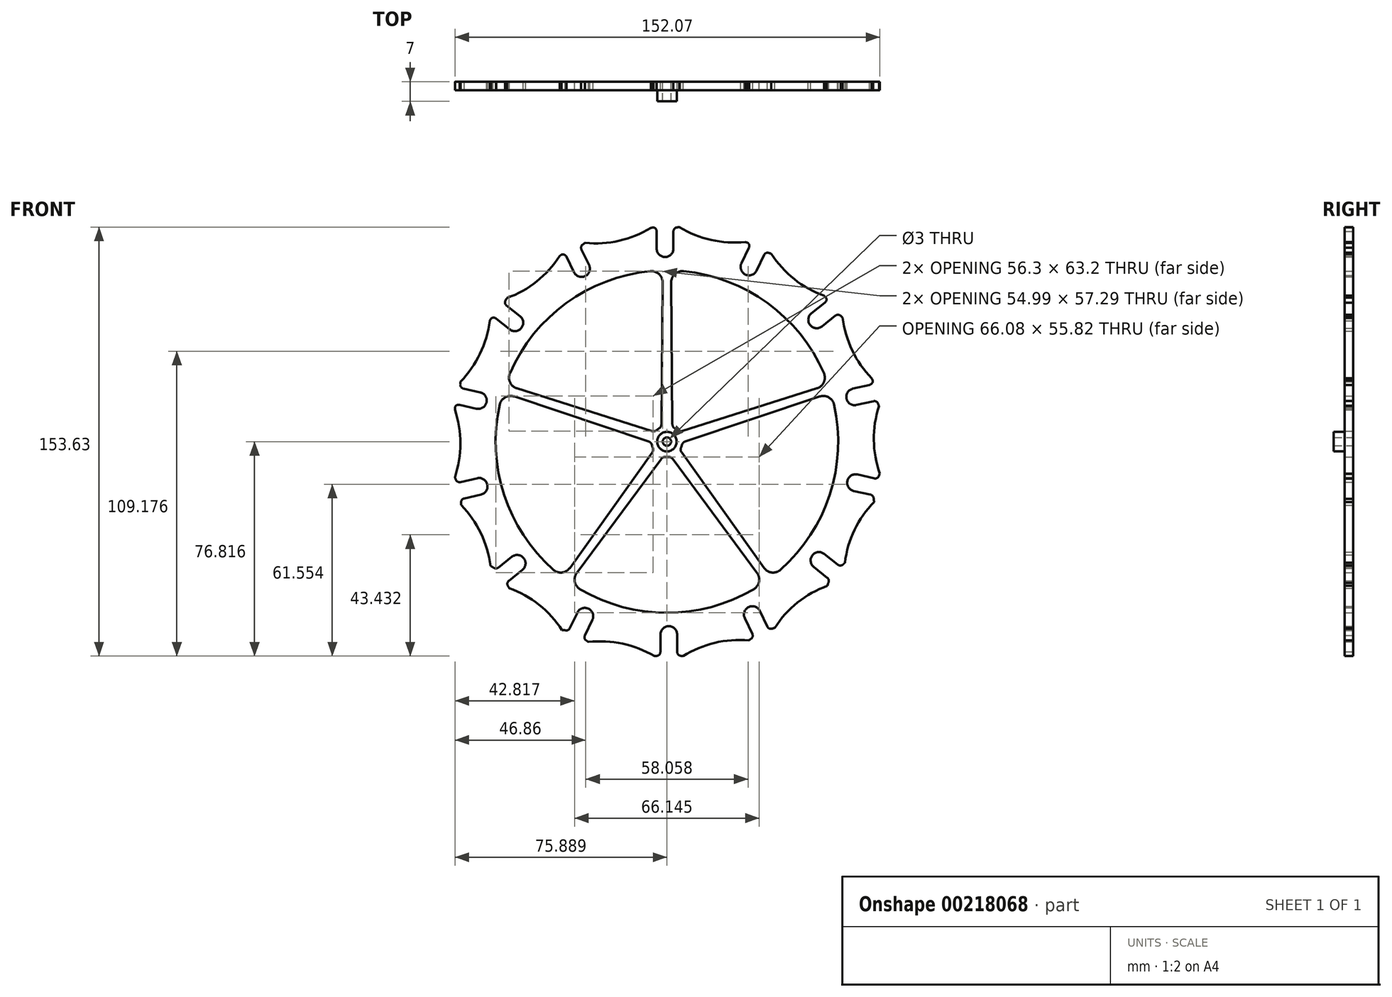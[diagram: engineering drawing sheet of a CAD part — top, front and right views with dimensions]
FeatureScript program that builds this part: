
annotation { "Feature Type Name" : "Feature", "Feature Type Description" : "" }
export const myFeature = defineFeature(function(context is Context, id is Id, definition is map)
    precondition{}
    {
        {
            var Q0;
            Q0=qCreatedBy(makeId("Front.planeOp"),FACE);
            var sketch = newSketch(context, id + "F0", { "sketchPlane" : qUnion([Q0])});
            skCircle(sketch, "E0", {"center": v(-22.2, -31.98) * mm, "radius": 2 * mm});
            skCircle(sketch, "E1", {"center": v(-22.2, -71.34) * mm, "radius": 1.5 * mm});
            skPoint(sketch, "E2.startSnap0", {"position": v(-22.24, -28.34) * mm});
            skPoint(sketch, "E3.orphan", {"position": v(-21.48, -28.34) * mm});
            skCircle(sketch, "E4", {"center": v(-22.2, -71.34) * mm, "radius": 7.5 * mm});
            skCircle(sketch, "E5", {"center": v(-22.2, -71.34) * mm, "radius": 2.5 * mm});
            skArc(sketch, "E6", {"start": v(-26.44, -36.03) * mm, "mid": v(-26.89, -36.09) * mm, "end": v(-27.34, -36.15) * mm});
            skArc(sketch, "E7.1.1", {"start": v(7.2, -29.99) * mm, "mid": v(6.81, -30.23) * mm, "end": v(6.43, -30.49) * mm});
            skArc(sketch, "E7.2.1", {"start": v(34.87, -9.95) * mm, "mid": v(34.73, -10.46) * mm, "end": v(34.6, -10.96) * mm});
            skArc(sketch, "E7.4.1", {"start": v(52.7, 54.24) * mm, "mid": v(52.87, 53.82) * mm, "end": v(53.03, 53.4) * mm});
            skPoint(sketch, "E7.center", {"position": v(-22.86, 40.67) * mm});
            skLineSegment(sketch, "E8", {"start": v(-25.2, -28.42) * mm, "end": v(-25.2, -34.62) * mm});
            skLineSegment(sketch, "E9.MirrorCS", {"start": v(-19.2, -28.42) * mm, "end": v(-19.2, -34.6) * mm});
            skArc(sketch, "E10", {"start": v(-19.2, -28.42) * mm, "mid": v(-22.2, -25.42) * mm, "end": v(-25.2, -28.42) * mm});
            skPoint(sketch, "E11.orphan", {"position": v(-25.2, -27.08) * mm});
            skPoint(sketch, "E12.orphan", {"position": v(-19.2, -27.02) * mm});
            skArc(sketch, "E13", {"start": v(-26.44, -36.03) * mm, "mid": v(-25.55, -35.56) * mm, "end": v(-25.2, -34.62) * mm});
            skPoint(sketch, "E14.orphan", {"position": v(-25.2, -35.93) * mm});
            skArc(sketch, "E15.MirrorCS", {"start": v(-17.94, -36.03) * mm, "mid": v(-18.84, -35.55) * mm, "end": v(-19.2, -34.6) * mm});
            skArc(sketch, "E16.1.0", {"start": v(10.42, -19.99) * mm, "mid": v(6.42, -18.59) * mm, "end": v(5.02, -22.6) * mm});
            skLineSegment(sketch, "E16.1.1", {"start": v(5.02, -22.6) * mm, "end": v(7.7, -28.18) * mm});
            skArc(sketch, "E16.1.2", {"start": v(7.2, -29.99) * mm, "mid": v(7.8, -29.18) * mm, "end": v(7.7, -28.18) * mm});
            skArc(sketch, "E16.1.3", {"start": v(14.85, -26.3) * mm, "mid": v(13.83, -26.26) * mm, "end": v(13.1, -25.55) * mm});
            skLineSegment(sketch, "E16.1.4", {"start": v(10.42, -19.99) * mm, "end": v(13.1, -25.55) * mm});
            skArc(sketch, "E16.2.0", {"start": v(33.44, 0.46) * mm, "mid": v(29.23, -0.01) * mm, "end": v(29.7, -4.23) * mm});
            skLineSegment(sketch, "E16.2.1", {"start": v(29.7, -4.23) * mm, "end": v(34.55, -8.1) * mm});
            skArc(sketch, "E16.2.2", {"start": v(34.87, -9.95) * mm, "mid": v(35.06, -8.96) * mm, "end": v(34.55, -8.1) * mm});
            skArc(sketch, "E16.2.3", {"start": v(40.17, -3.3) * mm, "mid": v(39.23, -3.72) * mm, "end": v(38.27, -3.39) * mm});
            skLineSegment(sketch, "E16.2.4", {"start": v(33.44, 0.46) * mm, "end": v(38.27, -3.39) * mm});
            skArc(sketch, "E16.3.0", {"start": v(45.31, 28.87) * mm, "mid": v(41.72, 26.61) * mm, "end": v(43.98, 23.02) * mm});
            skLineSegment(sketch, "E16.3.1", {"start": v(43.98, 23.02) * mm, "end": v(50.02, 21.64) * mm});
            skArc(sketch, "E16.3.2", {"start": v(51.12, 20.11) * mm, "mid": v(50.86, 21.08) * mm, "end": v(50.02, 21.64) * mm});
            skArc(sketch, "E16.3.3", {"start": v(53, 28.4) * mm, "mid": v(52.34, 27.62) * mm, "end": v(51.33, 27.5) * mm});
            skLineSegment(sketch, "E16.3.4", {"start": v(45.31, 28.87) * mm, "end": v(51.33, 27.5) * mm});
            skArc(sketch, "E16.4.0", {"start": v(43.68, 59.62) * mm, "mid": v(41.42, 56.02) * mm, "end": v(45.01, 53.77) * mm});
            skLineSegment(sketch, "E16.4.1", {"start": v(45.01, 53.77) * mm, "end": v(51.06, 55.15) * mm});
            skArc(sketch, "E16.4.2", {"start": v(52.7, 54.24) * mm, "mid": v(52.06, 55) * mm, "end": v(51.06, 55.15) * mm});
            skArc(sketch, "E16.4.3", {"start": v(50.82, 62.53) * mm, "mid": v(50.55, 61.54) * mm, "end": v(49.7, 61) * mm});
            skLineSegment(sketch, "E16.4.4", {"start": v(43.68, 59.62) * mm, "end": v(49.7, 61) * mm});
            skArc(sketch, "E16.5.0", {"start": v(28.87, 86.6) * mm, "mid": v(28.4, 82.4) * mm, "end": v(32.6, 81.92) * mm});
            skLineSegment(sketch, "E16.5.1", {"start": v(32.6, 81.92) * mm, "end": v(37.46, 85.79) * mm});
            skArc(sketch, "E16.5.2", {"start": v(39.33, 85.69) * mm, "mid": v(38.41, 86.1) * mm, "end": v(37.46, 85.79) * mm});
            skArc(sketch, "E16.5.3", {"start": v(34.04, 92.33) * mm, "mid": v(34.23, 91.33) * mm, "end": v(33.7, 90.46) * mm});
            skLineSegment(sketch, "E16.5.4", {"start": v(28.87, 86.6) * mm, "end": v(33.7, 90.46) * mm});
            skArc(sketch, "E16.6.0", {"start": v(3.8, 104.5) * mm, "mid": v(5.2, 100.5) * mm, "end": v(9.21, 101.9) * mm});
            skLineSegment(sketch, "E16.6.1", {"start": v(9.21, 101.9) * mm, "end": v(11.9, 107.49) * mm});
            skArc(sketch, "E16.6.2", {"start": v(13.64, 108.21) * mm, "mid": v(12.63, 108.18) * mm, "end": v(11.9, 107.49) * mm});
            skArc(sketch, "E16.6.3", {"start": v(5.99, 111.9) * mm, "mid": v(6.6, 111.08) * mm, "end": v(6.49, 110.06) * mm});
            skLineSegment(sketch, "E16.6.4", {"start": v(3.8, 104.5) * mm, "end": v(6.49, 110.06) * mm});
            skArc(sketch, "E16.7.0", {"start": v(-26.53, 109.75) * mm, "mid": v(-23.53, 106.75) * mm, "end": v(-20.53, 109.75) * mm});
            skLineSegment(sketch, "E16.7.1", {"start": v(-20.53, 109.75) * mm, "end": v(-20.53, 115.96) * mm});
            skArc(sketch, "E16.7.2", {"start": v(-19.28, 117.36) * mm, "mid": v(-20.17, 116.9) * mm, "end": v(-20.53, 115.96) * mm});
            skArc(sketch, "E16.7.3", {"start": v(-27.78, 117.36) * mm, "mid": v(-26.88, 116.88) * mm, "end": v(-26.53, 115.92) * mm});
            skLineSegment(sketch, "E16.7.4", {"start": v(-26.53, 109.75) * mm, "end": v(-26.53, 115.92) * mm});
            skArc(sketch, "E16.8.0", {"start": v(-56.14, 101.32) * mm, "mid": v(-52.14, 99.92) * mm, "end": v(-50.74, 103.92) * mm});
            skLineSegment(sketch, "E16.8.1", {"start": v(-50.74, 103.92) * mm, "end": v(-53.43, 109.51) * mm});
            skArc(sketch, "E16.8.2", {"start": v(-52.92, 111.32) * mm, "mid": v(-53.51, 110.51) * mm, "end": v(-53.43, 109.51) * mm});
            skArc(sketch, "E16.8.3", {"start": v(-60.57, 107.63) * mm, "mid": v(-59.55, 107.6) * mm, "end": v(-58.82, 106.88) * mm});
            skLineSegment(sketch, "E16.8.4", {"start": v(-56.14, 101.32) * mm, "end": v(-58.82, 106.88) * mm});
            skArc(sketch, "E16.9.0", {"start": v(-79.16, 80.87) * mm, "mid": v(-74.95, 81.35) * mm, "end": v(-75.42, 85.56) * mm});
            skLineSegment(sketch, "E16.9.1", {"start": v(-75.42, 85.56) * mm, "end": v(-80.27, 89.43) * mm});
            skArc(sketch, "E16.9.2", {"start": v(-80.6, 91.28) * mm, "mid": v(-80.78, 90.3) * mm, "end": v(-80.27, 89.43) * mm});
            skArc(sketch, "E16.9.3", {"start": v(-85.9, 84.64) * mm, "mid": v(-84.95, 85.05) * mm, "end": v(-83.99, 84.72) * mm});
            skLineSegment(sketch, "E16.9.4", {"start": v(-79.16, 80.87) * mm, "end": v(-83.99, 84.72) * mm});
            skArc(sketch, "E16.10.0", {"start": v(-91.03, 52.46) * mm, "mid": v(-87.44, 54.72) * mm, "end": v(-89.7, 58.31) * mm});
            skLineSegment(sketch, "E16.10.1", {"start": v(-89.7, 58.31) * mm, "end": v(-95.74, 59.7) * mm});
            skArc(sketch, "E16.10.2", {"start": v(-96.84, 61.22) * mm, "mid": v(-96.58, 60.25) * mm, "end": v(-95.74, 59.7) * mm});
            skArc(sketch, "E16.10.3", {"start": v(-98.73, 52.94) * mm, "mid": v(-98.06, 53.7) * mm, "end": v(-97.05, 53.83) * mm});
            skLineSegment(sketch, "E16.10.4", {"start": v(-91.03, 52.46) * mm, "end": v(-97.05, 53.83) * mm});
            skArc(sketch, "E16.11.0", {"start": v(-89.4, 21.71) * mm, "mid": v(-87.14, 25.3) * mm, "end": v(-90.73, 27.56) * mm});
            skLineSegment(sketch, "E16.11.1", {"start": v(-90.73, 27.56) * mm, "end": v(-96.78, 26.18) * mm});
            skArc(sketch, "E16.11.2", {"start": v(-98.43, 27.09) * mm, "mid": v(-97.78, 26.32) * mm, "end": v(-96.78, 26.18) * mm});
            skArc(sketch, "E16.11.3", {"start": v(-96.54, 18.8) * mm, "mid": v(-96.27, 19.79) * mm, "end": v(-95.42, 20.34) * mm});
            skLineSegment(sketch, "E16.11.4", {"start": v(-89.4, 21.71) * mm, "end": v(-95.42, 20.34) * mm});
            skArc(sketch, "E16.12.0", {"start": v(-74.59, -5.28) * mm, "mid": v(-74.11, -1.06) * mm, "end": v(-78.33, -0.59) * mm});
            skLineSegment(sketch, "E16.12.1", {"start": v(-78.33, -0.59) * mm, "end": v(-83.18, -4.46) * mm});
            skArc(sketch, "E16.12.2", {"start": v(-85.05, -4.36) * mm, "mid": v(-84.13, -4.76) * mm, "end": v(-83.18, -4.46) * mm});
            skArc(sketch, "E16.12.3", {"start": v(-79.76, -11) * mm, "mid": v(-79.95, -10) * mm, "end": v(-79.41, -9.13) * mm});
            skLineSegment(sketch, "E16.12.4", {"start": v(-74.59, -5.28) * mm, "end": v(-79.41, -9.13) * mm});
            skArc(sketch, "E16.13.0", {"start": v(-49.53, -23.17) * mm, "mid": v(-50.93, -19.17) * mm, "end": v(-54.94, -20.57) * mm});
            skLineSegment(sketch, "E16.13.1", {"start": v(-54.94, -20.57) * mm, "end": v(-57.63, -26.16) * mm});
            skArc(sketch, "E16.13.2", {"start": v(-59.36, -26.88) * mm, "mid": v(-58.36, -26.85) * mm, "end": v(-57.63, -26.16) * mm});
            skArc(sketch, "E16.13.3", {"start": v(-51.7, -30.57) * mm, "mid": v(-52.31, -29.75) * mm, "end": v(-52.2, -28.73) * mm});
            skLineSegment(sketch, "E16.13.4", {"start": v(-49.53, -23.17) * mm, "end": v(-52.2, -28.73) * mm});
            skPoint(sketch, "E17.trimOffspring.start.orphan", {"position": v(-19.2, -35.87) * mm});
            skPoint(sketch, "E18.orphan", {"position": v(-11.1, -37.55) * mm});
            skArc(sketch, "E19.trimOffspring", {"start": v(6.43, -30.49) * mm, "mid": v(-5.77, -31.4) * mm, "end": v(-17.04, -36.15) * mm});
            skArc(sketch, "E20.trimOffspring", {"start": v(15.71, -26.02) * mm, "mid": v(15.28, -26.16) * mm, "end": v(14.85, -26.3) * mm});
            skArc(sketch, "E21.trimOffspring", {"start": v(34.6, -10.96) * mm, "mid": v(23.92, -16.95) * mm, "end": v(15.71, -26.02) * mm});
            skArc(sketch, "E22.trimOffspring", {"start": v(40.83, -2.68) * mm, "mid": v(40.5, -3) * mm, "end": v(40.17, -3.3) * mm});
            skArc(sketch, "E23.trimOffspring", {"start": v(51.12, 20.11) * mm, "mid": v(51.2, 19.6) * mm, "end": v(51.3, 19.08) * mm});
            skArc(sketch, "E24.trimOffspring", {"start": v(53.32, 29.25) * mm, "mid": v(53.16, 28.82) * mm, "end": v(53, 28.4) * mm});
            skArc(sketch, "E25.trimOffspring", {"start": v(51.3, 19.08) * mm, "mid": v(44.29, 9.05) * mm, "end": v(40.83, -2.68) * mm});
            skArc(sketch, "E26.trimOffspring", {"start": v(53.03, 53.4) * mm, "mid": v(51.2, 41.3) * mm, "end": v(53.32, 29.25) * mm});
            skArc(sketch, "E27.trimOffspring", {"start": v(50.47, 63.3) * mm, "mid": v(50.64, 62.91) * mm, "end": v(50.82, 62.53) * mm});
            skArc(sketch, "E28.trimOffspring", {"start": v(39.99, 85.06) * mm, "mid": v(43.45, 73.32) * mm, "end": v(50.47, 63.3) * mm});
            skArc(sketch, "E29.trimOffspring", {"start": v(33.38, 92.88) * mm, "mid": v(33.7, 92.6) * mm, "end": v(34.04, 92.33) * mm});
            skArc(sketch, "E30.trimOffspring", {"start": v(13.64, 108.21) * mm, "mid": v(14.07, 108.07) * mm, "end": v(14.5, 107.93) * mm});
            skArc(sketch, "E31.trimOffspring", {"start": v(14.5, 107.93) * mm, "mid": v(22.71, 98.86) * mm, "end": v(33.38, 92.88) * mm});
            skArc(sketch, "E32.trimOffspring", {"start": v(5.16, 112.1) * mm, "mid": v(5.57, 112) * mm, "end": v(5.99, 111.9) * mm});
            skArc(sketch, "E33.trimOffspring", {"start": v(-19.28, 117.36) * mm, "mid": v(-18.83, 117.42) * mm, "end": v(-18.38, 117.48) * mm});
            skArc(sketch, "E34.trimOffspring", {"start": v(-18.38, 117.48) * mm, "mid": v(-7.05, 112.87) * mm, "end": v(5.16, 112.1) * mm});
            skArc(sketch, "E35.trimOffspring", {"start": v(-28.61, 117.2) * mm, "mid": v(-28.2, 117.27) * mm, "end": v(-27.78, 117.36) * mm});
            skArc(sketch, "E36.trimOffspring", {"start": v(-52.92, 111.32) * mm, "mid": v(-52.53, 111.57) * mm, "end": v(-52.15, 111.82) * mm});
            skArc(sketch, "E37.trimOffspring", {"start": v(-52.15, 111.82) * mm, "mid": v(-39.95, 112.58) * mm, "end": v(-28.61, 117.2) * mm});
            skArc(sketch, "E38.trimOffspring", {"start": v(-61.25, 107.12) * mm, "mid": v(-60.9, 107.37) * mm, "end": v(-60.57, 107.63) * mm});
            skArc(sketch, "E39.trimOffspring", {"start": v(-80.6, 91.28) * mm, "mid": v(-80.36, 91.67) * mm, "end": v(-80.13, 92.06) * mm});
            skArc(sketch, "E40.trimOffspring", {"start": v(-80.13, 92.06) * mm, "mid": v(-69.46, 98.05) * mm, "end": v(-61.25, 107.12) * mm});
            skArc(sketch, "E41.trimOffspring", {"start": v(-86.28, 83.88) * mm, "mid": v(-86.08, 84.26) * mm, "end": v(-85.9, 84.64) * mm});
            skArc(sketch, "E42.trimOffspring", {"start": v(-96.84, 61.22) * mm, "mid": v(-96.8, 61.67) * mm, "end": v(-96.75, 62.13) * mm});
            skArc(sketch, "E43.trimOffspring", {"start": v(-96.75, 62.13) * mm, "mid": v(-89.74, 72.15) * mm, "end": v(-86.28, 83.88) * mm});
            skArc(sketch, "E44.trimOffspring", {"start": v(-98.75, 52.09) * mm, "mid": v(-98.74, 52.51) * mm, "end": v(-98.73, 52.94) * mm});
            skArc(sketch, "E45.trimOffspring", {"start": v(-98.43, 27.09) * mm, "mid": v(-98.59, 27.51) * mm, "end": v(-98.75, 27.94) * mm});
            skArc(sketch, "E46.trimOffspring", {"start": v(-98.75, 27.94) * mm, "mid": v(-96.78, 40.01) * mm, "end": v(-98.75, 52.09) * mm});
            skArc(sketch, "E47.trimOffspring", {"start": v(-96.46, 17.9) * mm, "mid": v(-96.5, 18.35) * mm, "end": v(-96.54, 18.8) * mm});
            skArc(sketch, "E48.trimOffspring", {"start": v(-85.05, -4.36) * mm, "mid": v(-85.52, -4.1) * mm, "end": v(-85.98, -3.86) * mm});
            skArc(sketch, "E49.trimOffspring", {"start": v(-85.98, -3.86) * mm, "mid": v(-89.44, 7.88) * mm, "end": v(-96.46, 17.9) * mm});
            skArc(sketch, "E50.trimOffspring", {"start": v(-79.29, -11.78) * mm, "mid": v(-79.52, -11.39) * mm, "end": v(-79.76, -11) * mm});
            skArc(sketch, "E51.trimOffspring", {"start": v(-60.41, -26.83) * mm, "mid": v(-68.62, -17.76) * mm, "end": v(-79.29, -11.78) * mm});
            skArc(sketch, "E52.trimOffspring", {"start": v(-59.36, -26.88) * mm, "mid": v(-59.89, -26.85) * mm, "end": v(-60.41, -26.83) * mm});
            skArc(sketch, "E53.trimOffspring", {"start": v(-50.95, -31.07) * mm, "mid": v(-51.33, -30.82) * mm, "end": v(-51.7, -30.57) * mm});
            skArc(sketch, "E54.trimOffspring", {"start": v(-27.34, -36.15) * mm, "mid": v(-38.73, -31.68) * mm, "end": v(-50.95, -31.07) * mm});
            skArc(sketch, "E55.trimOffspring", {"start": v(-17.04, -36.15) * mm, "mid": v(-17.5, -36.09) * mm, "end": v(-17.94, -36.03) * mm});
            skPoint(sketch, "E56.orphan", {"position": v(-33.29, -37.55) * mm});
            skLineSegment(sketch, "E57", {"start": v(39.33, 85.69) * mm, "end": v(39.99, 85.06) * mm});
            skCircle(sketch, "E58", {"center": v(-22.86, 40.67) * mm, "radius": 1.5 * mm});
            skCircle(sketch, "E59", {"center": v(-22.86, 40.67) * mm, "radius": 3.5 * mm});
            skArc(sketch, "E60", {"start": v(-28.22, 39.42) * mm, "mid": v(-28.1, 38.97) * mm, "end": v(-27.93, 38.53) * mm});
            skLineSegment(sketch, "E61", {"start": v(-23.53, 110.93) * mm, "end": v(-23.53, 109.75) * mm});
            skArc(sketch, "E62", {"start": v(-82.71, 53.89) * mm, "mid": v(-81.15, 21.73) * mm, "end": v(-63.5, -5.2) * mm});
            skLineSegment(sketch, "E63", {"start": v(-24.82, 46.93) * mm, "end": v(-24.4, 97.66) * mm});
            skLineSegment(sketch, "E64.trimOffspring", {"start": v(-23.53, 109.75) * mm, "end": v(-23.53, 110.93) * mm});
            skLineSegment(sketch, "E65.MirrorCS", {"start": v(-20.9, 46.93) * mm, "end": v(-21.33, 97.66) * mm});
            skLineSegment(sketch, "E66.MirrorCS", {"start": v(-20.74, 35.68) * mm, "end": v(-20.74, 35.6) * mm});
            skLineSegment(sketch, "E67.MirrorCS", {"start": v(-24.67, 35.56) * mm, "end": v(-24.67, 35.47) * mm});
            skLineSegment(sketch, "E68.trimOffspring", {"start": v(-22.2, -25.42) * mm, "end": v(-22.2, -31.98) * mm});
            skPoint(sketch, "E69.orphan", {"position": v(-19.51, -20.45) * mm});
            skLineSegment(sketch, "E70.trimOffspring", {"start": v(20.48, -2.67) * mm, "end": v(21.12, -3.31) * mm});
            skPoint(sketch, "E71.orphan", {"position": v(-8.62, 26.42) * mm});
            skPoint(sketch, "E72.orphan", {"position": v(-38.44, 26.42) * mm});
            skArc(sketch, "E73", {"start": v(-20.9, 46.93) * mm, "mid": v(-20.66, 46.04) * mm, "end": v(-20.02, 45.37) * mm});
            skPoint(sketch, "E74.orphan", {"position": v(-20.9, 45.8) * mm});
            skArc(sketch, "E75.MirrorCS", {"start": v(-24.82, 46.93) * mm, "mid": v(-25.06, 46.04) * mm, "end": v(-25.7, 45.37) * mm});
            skPoint(sketch, "E76.orphan", {"position": v(-24.83, 45.8) * mm});
            skArc(sketch, "E77", {"start": v(-16.94, 101.67) * mm, "mid": v(-20.03, 100.64) * mm, "end": v(-21.33, 97.66) * mm});
            skPoint(sketch, "E78.orphan", {"position": v(-21.36, 101.94) * mm});
            skArc(sketch, "E79.MirrorCS", {"start": v(-28.78, 101.67) * mm, "mid": v(-25.7, 100.64) * mm, "end": v(-24.4, 97.66) * mm});
            skPoint(sketch, "E80.orphan", {"position": v(-24.36, 101.94) * mm});
            skArc(sketch, "E81.1.0", {"start": v(-82.71, 53.89) * mm, "mid": v(-80.78, 56.5) * mm, "end": v(-77.54, 56.82) * mm});
            skArc(sketch, "E81.1.1", {"start": v(-79.05, 65.15) * mm, "mid": v(-79.02, 61.9) * mm, "end": v(-76.59, 59.74) * mm});
            skLineSegment(sketch, "E81.1.2", {"start": v(-28.21, 44.46) * mm, "end": v(-76.59, 59.74) * mm});
            skLineSegment(sketch, "E81.1.3", {"start": v(-29.42, 40.74) * mm, "end": v(-77.54, 56.82) * mm});
            skArc(sketch, "E81.1.4", {"start": v(-29.42, 40.74) * mm, "mid": v(-28.65, 40.23) * mm, "end": v(-28.22, 39.42) * mm});
            skArc(sketch, "E81.1.5", {"start": v(-28.21, 44.46) * mm, "mid": v(-27.29, 44.42) * mm, "end": v(-26.46, 44.82) * mm});
            skArc(sketch, "E81.2.0", {"start": v(-53.93, -12.17) * mm, "mid": v(-55.82, -9.52) * mm, "end": v(-55.12, -6.34) * mm});
            skArc(sketch, "E81.2.1", {"start": v(-63.5, -5.2) * mm, "mid": v(-60.4, -6.19) * mm, "end": v(-57.6, -4.54) * mm});
            skLineSegment(sketch, "E81.2.2", {"start": v(-28.13, 36.75) * mm, "end": v(-57.6, -4.54) * mm});
            skLineSegment(sketch, "E81.2.3", {"start": v(-24.96, 34.45) * mm, "end": v(-55.12, -6.34) * mm});
            skArc(sketch, "E81.2.4", {"start": v(-24.96, 34.45) * mm, "mid": v(-24.24, 35.03) * mm, "end": v(-23.33, 35.19) * mm});
            skArc(sketch, "E81.2.5", {"start": v(-28.13, 36.75) * mm, "mid": v(-27.8, 37.61) * mm, "end": v(-27.93, 38.53) * mm});
            skArc(sketch, "E82.4.3.0", {"start": v(8.2, -12.17) * mm, "mid": v(10.1, -9.52) * mm, "end": v(9.4, -6.34) * mm});
            skLineSegment(sketch, "E82.8.3.0", {"start": v(-20.76, 34.45) * mm, "end": v(9.4, -6.34) * mm});
            skLineSegment(sketch, "E82.11.3.0", {"start": v(-17.6, 36.75) * mm, "end": v(11.88, -4.54) * mm});
            skArc(sketch, "E82.14.3.0", {"start": v(-17.6, 36.75) * mm, "mid": v(-17.93, 37.61) * mm, "end": v(-17.8, 38.53) * mm});
            skArc(sketch, "E82.17.3.0", {"start": v(17.79, -5.2) * mm, "mid": v(14.69, -6.19) * mm, "end": v(11.88, -4.54) * mm});
            skArc(sketch, "E82.18.3.0", {"start": v(-20.76, 34.45) * mm, "mid": v(-21.48, 35.03) * mm, "end": v(-22.4, 35.19) * mm});
            skArc(sketch, "E82.4.4.0", {"start": v(36.99, 53.89) * mm, "mid": v(35.06, 56.5) * mm, "end": v(31.82, 56.82) * mm});
            skLineSegment(sketch, "E82.8.4.0", {"start": v(-16.3, 40.74) * mm, "end": v(31.82, 56.82) * mm});
            skLineSegment(sketch, "E82.11.4.0", {"start": v(-17.5, 44.46) * mm, "end": v(30.87, 59.74) * mm});
            skArc(sketch, "E82.14.4.0", {"start": v(-17.5, 44.46) * mm, "mid": v(-18.43, 44.42) * mm, "end": v(-19.26, 44.82) * mm});
            skArc(sketch, "E82.17.4.0", {"start": v(33.33, 65.15) * mm, "mid": v(33.3, 61.9) * mm, "end": v(30.87, 59.74) * mm});
            skArc(sketch, "E82.18.4.0", {"start": v(-16.3, 40.74) * mm, "mid": v(-17.07, 40.23) * mm, "end": v(-17.5, 39.42) * mm});
            skArc(sketch, "E83.trimOffspring", {"start": v(33.33, 65.15) * mm, "mid": v(13.17, 90.25) * mm, "end": v(-16.94, 101.67) * mm});
            skPoint(sketch, "E84.MirrorCS.start.orphan", {"position": v(20.43, 85.3) * mm});
            skPoint(sketch, "E85.start.orphan", {"position": v(-67.5, 85.3) * mm});
            skArc(sketch, "E86.trimOffspring", {"start": v(-28.78, 101.67) * mm, "mid": v(-58.89, 90.25) * mm, "end": v(-79.05, 65.15) * mm});
            skPoint(sketch, "E87.trimOffspring.end.orphan", {"position": v(-22.86, 46.17) * mm});
            skArc(sketch, "E88.trimOffspring", {"start": v(17.79, -5.2) * mm, "mid": v(35.43, 21.73) * mm, "end": v(36.99, 53.89) * mm});
            skArc(sketch, "E89.trimOffspring", {"start": v(-53.93, -12.17) * mm, "mid": v(-22.86, -20.63) * mm, "end": v(8.2, -12.17) * mm});
            skPoint(sketch, "E90.orphan", {"position": v(-22.86, 101.96) * mm});
            skArc(sketch, "E91.trimOffspring", {"start": v(-23.33, 35.19) * mm, "mid": v(-22.86, 35.17) * mm, "end": v(-22.4, 35.19) * mm});
            skArc(sketch, "E92.trimOffspring", {"start": v(-17.8, 38.53) * mm, "mid": v(-17.63, 38.97) * mm, "end": v(-17.5, 39.42) * mm});
            skArc(sketch, "E93.trimOffspring", {"start": v(-19.26, 44.82) * mm, "mid": v(-19.63, 45.12) * mm, "end": v(-20.02, 45.37) * mm});
            skArc(sketch, "E94.trimOffspring", {"start": v(-25.7, 45.37) * mm, "mid": v(-26.1, 45.12) * mm, "end": v(-26.46, 44.82) * mm});
            skCircle(sketch, "E95", {"center": v(-22.86, 40.67) * mm, "radius": 112 * mm});
            skLineSegment(sketch, "E96.trimOffspring", {"start": v(-39.35, -31.55) * mm, "end": v(-40.42, -36.26) * mm});
            skSolve(sketch);
        }
        {
            var Q0;
            Q0=makeQuery(id+"F0.imprint","IMPRINT",FACE,{"disambiguationData":[TD([[makeQuery(id+"F0.imprint","IMPRINT",EDGE,{"derivedFrom":sQuery(id+"F0.wireOp",EDGE,"E6")}),-1.0]])]});
            extrude(context, id + "F1", {"entities" : qUnion([Q0]), "depth" : 3 * mm});
        }
        {
            var Q0;
            Q0=makeQuery(id+"F0.imprint","IMPRINT",FACE,{"disambiguationData":[TD([[makeQuery(id+"F0.imprint","IMPRINT",EDGE,{"derivedFrom":sQuery(id+"F0.wireOp",EDGE,"E58")}),-1.0]])]});
            extrude(context, id + "F2", {"entities" : qUnion([Q0]), "operationType" : NewBodyOperationType.ADD, "depth" : 7 * mm});
        }
    });
